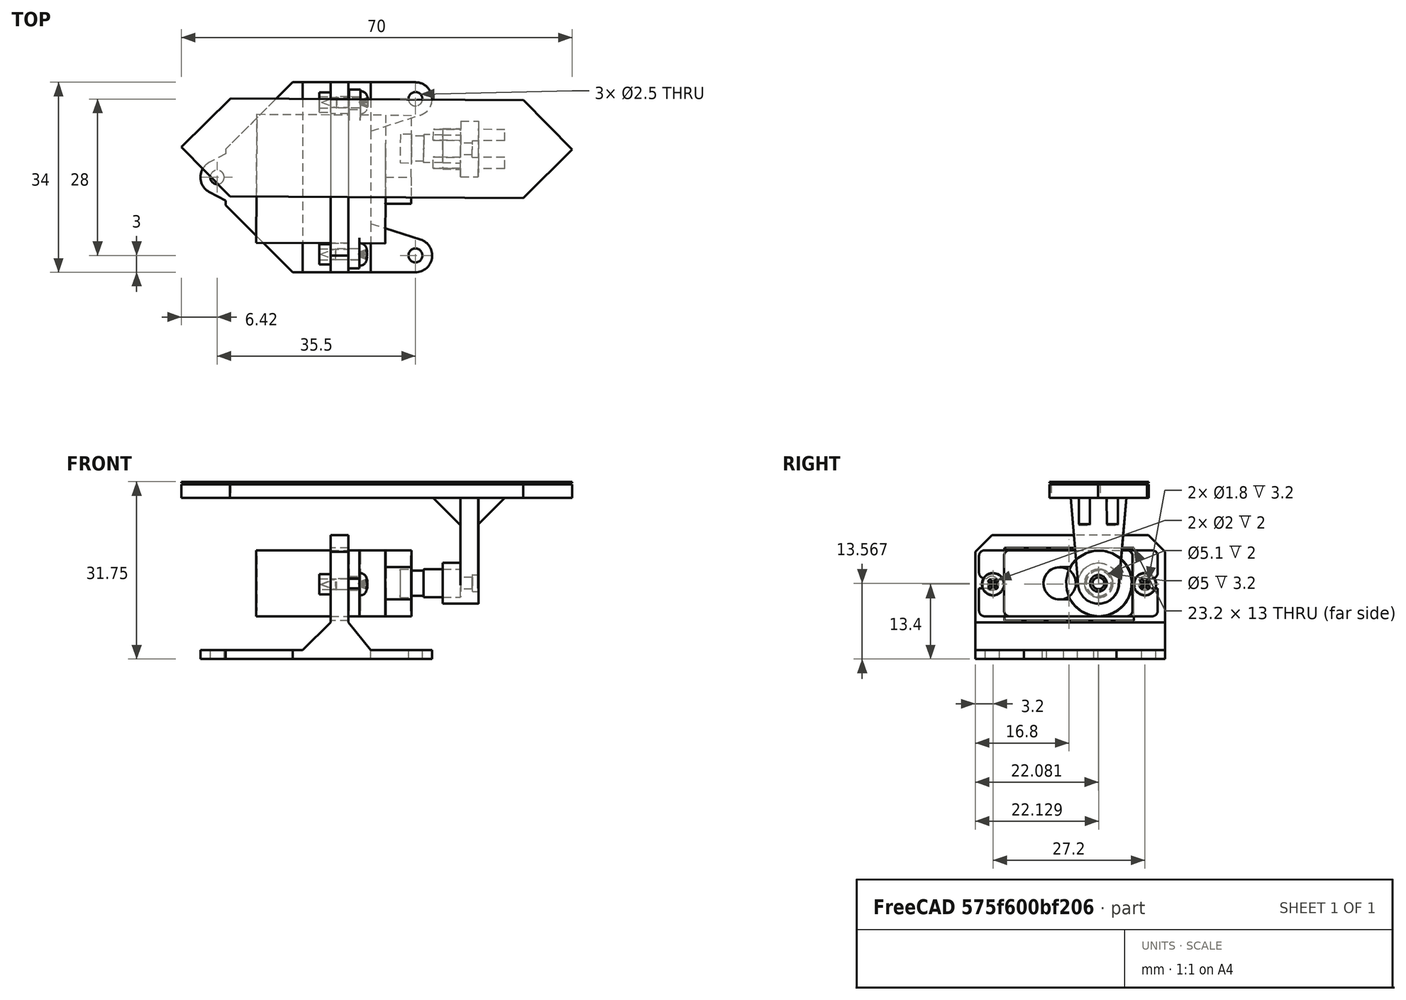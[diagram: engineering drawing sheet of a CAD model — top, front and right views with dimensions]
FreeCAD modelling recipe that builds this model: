
FCSTD DOCUMENT  (FreeCAD 0.20R29603 (Git))
Label: Segment_70x17_assembly
License: All rights reserved
LicenseURL: http://en.wikipedia.org/wiki/All_rights_reserved
objects: App::FeaturePython×10, Part::FeaturePython×7
note: 7 computed .brp shape members not serialized (recipe doc carries the construction recipe); baked Part::Feature solids carry a one-line shape summary decoded from their .brp

FEATURE [Part::FeaturePython] b_SG90_Holder_001_  label="SG90_Holder_001"  # a2plus imported part (geometry in sourceFile) (typed FeaturePython)
  a2p_Version = 0.4.60i
  fixedPosition = true
  objectType = a2pPart
  sourceFile = ./SG90_Holder.FCStd
  subassemblyImport = false
  timeLastImport = 1.67534e+09
  updateColors = true
FEATURE [Part::FeaturePython] b_Segment_70x17_001_  label="Segment_70x17_001"  # a2plus imported part (geometry in sourceFile) (typed FeaturePython)
  Placement = pos=(5.08411,-11.826,31.2674) rot=(0.999996,-0.002985,-1e-06;3.14083rad)
  a2p_Version = 0.4.60i
  fixedPosition = false
  objectType = a2pPart
  sourceFile = ./Segment_70x17.FCStd
  subassemblyImport = false
  timeLastImport = 1.67638e+09
  updateColors = true
FEATURE [Part::FeaturePython] b_SG90_Corpo_001_  label="SG90_Corpo_001"  # a2plus imported part (geometry in sourceFile) (typed FeaturePython)
  Placement = pos=(-16.4484,-17.2111,13.5674) rot=(0.579648,0.576198,0.576198;2.09095rad)
  a2p_Version = 0.4.60i
  fixedPosition = false
  objectType = a2pPart
  sourceFile = ./../../SG90/SG90_Corpo.FCStd
  subassemblyImport = false
  timeLastImport = 1.67517e+09
  updateColors = true
FEATURE [Part::FeaturePython] b_SG90_Eixo_001_  label="SG90_Eixo_001"  # a2plus imported part (geometry in sourceFile) (typed FeaturePython)
  Placement = pos=(11.2839,-11.8766,13.5674) rot=(0.7071,-0.003095,0.707106;3.13934rad)
  a2p_Version = 0.4.60i
  fixedPosition = false
  objectType = a2pPart
  sourceFile = ./../../SG90/SG90_Eixo.FCStd
  subassemblyImport = false
  timeLastImport = 1.67508e+09
  updateColors = true
FEATURE [Part::FeaturePython] Screw  label="2 mmx7-Screw"  # Fasteners workbench fastener (typed FeaturePython)
  Placement = pos=(2.13652,-3.61025,13.4074) rot=(0.001337,0.999998,-0.001405;1.56883rad)
  diameter = 1
  invert = false
  leftHanded = false
  length = 0
  lengthCustom = 7
  matchOuter = false
  offset = 0
  thread = false
  type = 28
FEATURE [Part::FeaturePython] Screw001  label="2 mmx7-Screw001"  # Fasteners workbench fastener (typed FeaturePython)
  Placement = pos=(1.98501,-30.8098,13.4071) rot=(0.001337,0.999998,-0.001405;1.56883rad)
  diameter = 1
  invert = false
  leftHanded = false
  length = 0
  lengthCustom = 7
  matchOuter = false
  offset = 0
  thread = false
  type = 28
FEATURE [Part::FeaturePython] b_FacePlate_70x17_001_  label="FacePlate_70x17_001"  # a2plus imported part (geometry in sourceFile) (typed FeaturePython)
  Placement = pos=(5.08409,-11.8258,31.5383) rot=(-0.127152,0.000345,-0.991883;0.006018rad)
  a2p_Version = 0.4.60i
  fixedPosition = false
  objectType = a2pPart
  sourceFile = ./FacePlate_70x17.FCStd
  subassemblyImport = false
  timeLastImport = 1.67528e+09
  updateColors = true
FEATURE [App::FeaturePython] planeCoincident_006  label="planeCoincident_006__Segment_70x17_001"  # a2plus constraint (typed FeaturePython)
  Object1 = b_FacePlate_70x17_001_
  Object2 = b_Segment_70x17_001_
  ParentTreeObject = -> b_FacePlate_70x17_001_
  SubElement1 = Face4
  SubElement2 = Face1
  Suppressed = false
  Type = plane
  directionConstraint = 1
  offset = 0
FEATURE [App::FeaturePython] planeCoincident_006_mirror  label="planeCoincident_006__FacePlate_70x17_001"  # a2plus constraint (typed FeaturePython)
  Object1 = b_FacePlate_70x17_001_
  Object2 = b_Segment_70x17_001_
  ParentTreeObject = -> b_Segment_70x17_001_
  SubElement1 = Face4
  SubElement2 = Face1
  Suppressed = false
  Type = plane
  directionConstraint = 1
  offset = 0
FEATURE [App::FeaturePython] planeCoincident_007  label="planeCoincident_007__Segment_70x17_001"  # a2plus constraint (typed FeaturePython)
  Object1 = b_FacePlate_70x17_001_
  Object2 = b_Segment_70x17_001_
  ParentTreeObject = -> b_FacePlate_70x17_001_
  SubElement1 = Face5
  SubElement2 = Face2
  Suppressed = false
  Type = plane
  directionConstraint = 1
  offset = 0
FEATURE [App::FeaturePython] planeCoincident_007_mirror  label="planeCoincident_007__FacePlate_70x17_001"  # a2plus constraint (typed FeaturePython)
  Object1 = b_FacePlate_70x17_001_
  Object2 = b_Segment_70x17_001_
  ParentTreeObject = -> b_Segment_70x17_001_
  SubElement1 = Face5
  SubElement2 = Face2
  Suppressed = false
  Type = plane
  directionConstraint = 1
  offset = 0
FEATURE [App::FeaturePython] planesParallel_001  label="planesParallel_001__SG90_Corpo_001"  # a2plus constraint (typed FeaturePython)
  Object1 = b_SG90_Holder_001_
  Object2 = b_SG90_Corpo_001_
  ParentTreeObject = -> b_SG90_Holder_001_
  SubElement1 = Face24
  SubElement2 = Face24
  Suppressed = false
  Type = planesParallel
  directionConstraint = 1
FEATURE [App::FeaturePython] planesParallel_001_mirror  label="planesParallel_001__SG90_Holder_001"  # a2plus constraint (typed FeaturePython)
  Object1 = b_SG90_Holder_001_
  Object2 = b_SG90_Corpo_001_
  ParentTreeObject = -> b_SG90_Corpo_001_
  SubElement1 = Face24
  SubElement2 = Face24
  Suppressed = false
  Type = planesParallel
  directionConstraint = 1
FEATURE [App::FeaturePython] circularEdge_001  label="circularEdge_001__SG90_Eixo_001"  # a2plus constraint (typed FeaturePython)
  Object1 = b_SG90_Corpo_001_
  Object2 = b_SG90_Eixo_001_
  ParentTreeObject = -> b_SG90_Corpo_001_
  SubElement1 = Edge134
  SubElement2 = Edge6
  Suppressed = false
  Type = circularEdge
  directionConstraint = 0
  lockRotation = false
  offset = 0
FEATURE [App::FeaturePython] circularEdge_001_mirror  label="circularEdge_001__SG90_Corpo_001"  # a2plus constraint (typed FeaturePython)
  Object1 = b_SG90_Corpo_001_
  Object2 = b_SG90_Eixo_001_
  ParentTreeObject = -> b_SG90_Eixo_001_
  SubElement1 = Edge134
  SubElement2 = Edge6
  Suppressed = false
  Type = circularEdge
  directionConstraint = 0
  lockRotation = false
  offset = 0
FEATURE [App::FeaturePython] circularEdge_002  label="circularEdge_002__SG90_Eixo_001"  # a2plus constraint (typed FeaturePython)
  Object1 = b_Segment_70x17_001_
  Object2 = b_SG90_Eixo_001_
  ParentTreeObject = -> b_Segment_70x17_001_
  SubElement1 = Edge75
  SubElement2 = Edge3
  Suppressed = false
  Type = circularEdge
  directionConstraint = 1
  lockRotation = false
  offset = 0
FEATURE [App::FeaturePython] circularEdge_002_mirror  label="circularEdge_002__Segment_70x17_001"  # a2plus constraint (typed FeaturePython)
  Object1 = b_Segment_70x17_001_
  Object2 = b_SG90_Eixo_001_
  ParentTreeObject = -> b_SG90_Eixo_001_
  SubElement1 = Edge75
  SubElement2 = Edge3
  Suppressed = false
  Type = circularEdge
  directionConstraint = 1
  lockRotation = false
  offset = 0
